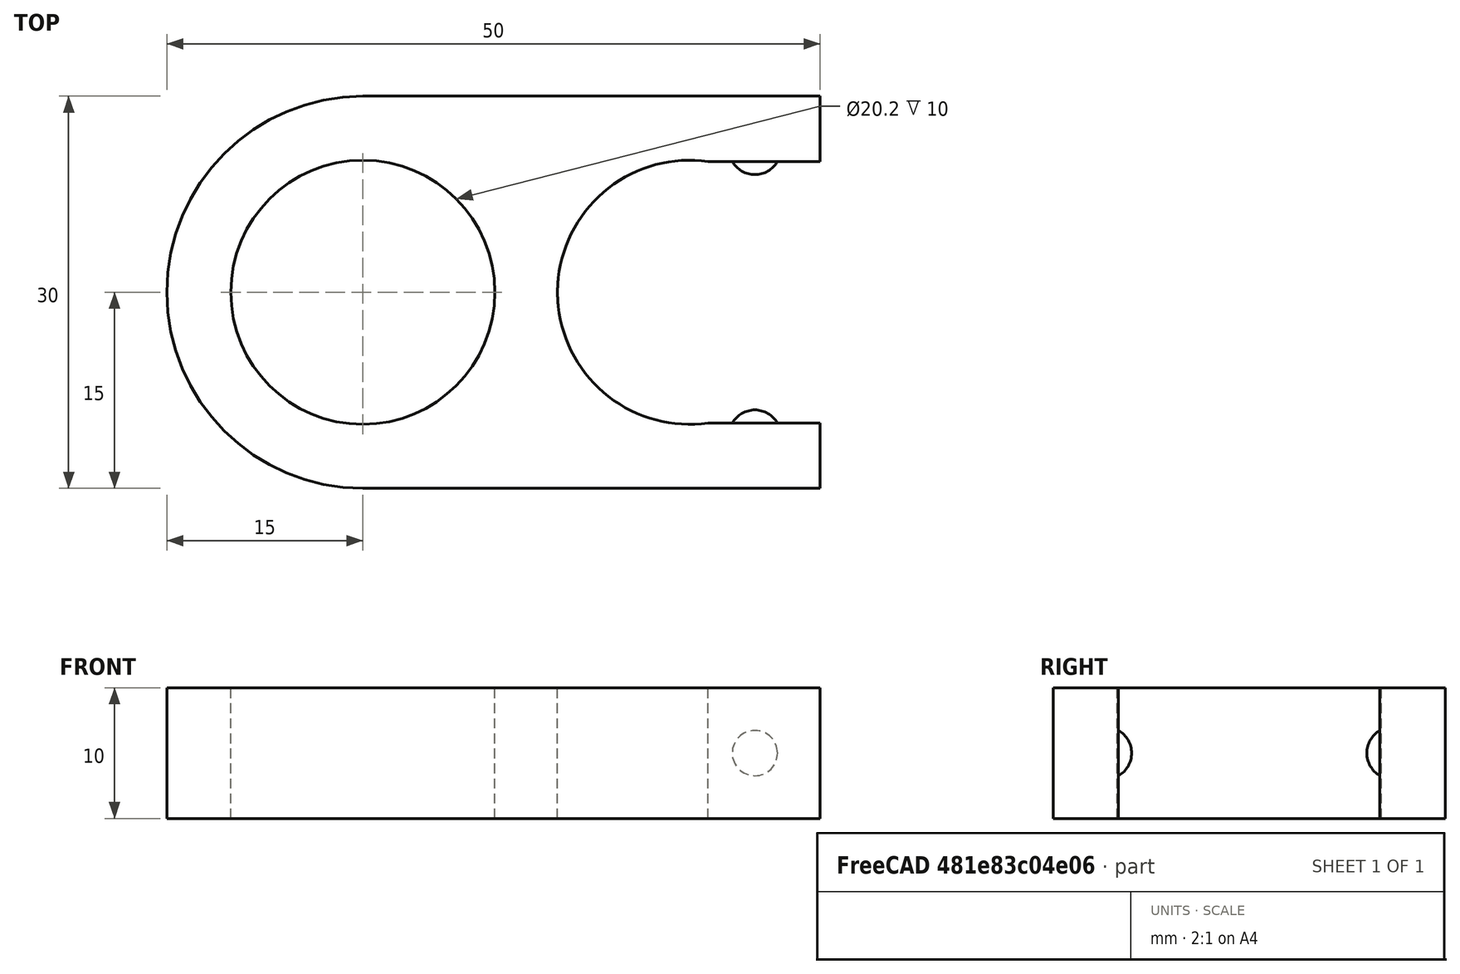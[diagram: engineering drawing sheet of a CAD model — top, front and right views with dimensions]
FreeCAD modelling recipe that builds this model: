
FCSTD DOCUMENT  (FreeCAD 0.17R13522 (Git))
Label: stand-holder
License: All rights reserved
LicenseURL: http://en.wikipedia.org/wiki/All_rights_reserved
objects: Part::Cylinder×3, Part::MultiFuse×3, Part::Box×2, Part::Sphere×2, Part::Cut×1
note: 11 computed .brp shape members not serialized (recipe doc carries the construction recipe); baked Part::Feature solids carry a one-line shape summary decoded from their .brp

FEATURE [Part::Box] Box  label="Cube"
  AttacherType = Attacher::AttachEngine3D
  Height = 10
  Length = 35
  Placement = pos=(0,-15,0) rot=(0,0,1;0rad)
  Width = 30
FEATURE [Part::Cylinder] Cylinder
  Angle = 360
  AttacherType = Attacher::AttachEngine3D
  Height = 10
  Radius = 15
FEATURE [Part::Cylinder] Cylinder001
  Angle = 360
  AttacherType = Attacher::AttachEngine3D
  Height = 10
  Radius = 10.1
FEATURE [Part::Cylinder] Cylinder002
  Angle = 360
  AttacherType = Attacher::AttachEngine3D
  Height = 10
  Placement = pos=(25,0,0) rot=(0,0,1;0rad)
  Radius = 10.1
FEATURE [Part::Box] Box001  label="Cube001"
  AttacherType = Attacher::AttachEngine3D
  Height = 10
  Length = 10
  Placement = pos=(25,-10,0) rot=(0,0,1;0rad)
  Width = 20
FEATURE [Part::MultiFuse] Fusion  label="Positive Fusion"
  Shapes = -> [Cylinder,Box]
FEATURE [Part::MultiFuse] Fusion001  label="Negative Fusion"
  Shapes = -> [Cylinder001,Cylinder002,Box001]
FEATURE [Part::Cut] Cut
  Base = -> Fusion
  Tool = -> Fusion001
FEATURE [Part::Sphere] Sphere
  Angle1 = -90
  Angle2 = 90
  Angle3 = 360
  AttacherType = Attacher::AttachEngine3D
  Placement = pos=(30,11,5) rot=(0,0,1;0rad)
  Radius = 2
FEATURE [Part::Sphere] Sphere001
  Angle1 = -90
  Angle2 = 90
  Angle3 = 360
  AttacherType = Attacher::AttachEngine3D
  Placement = pos=(30,-11,5) rot=(0,0,1;0rad)
  Radius = 2
FEATURE [Part::MultiFuse] Fusion002
  Shapes = -> [Sphere001,Sphere,Cut]
